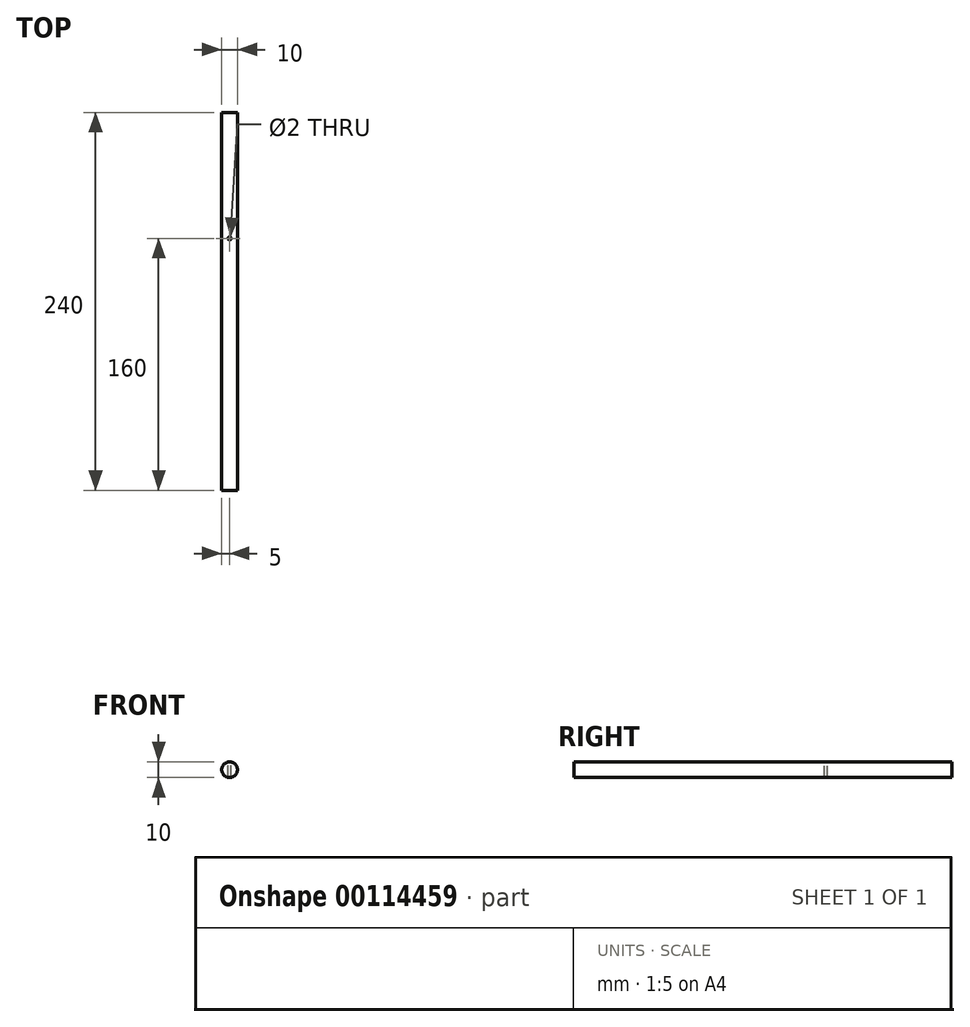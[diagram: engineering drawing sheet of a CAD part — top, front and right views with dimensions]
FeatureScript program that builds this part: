
annotation { "Feature Type Name" : "Feature", "Feature Type Description" : "" }
export const myFeature = defineFeature(function(context is Context, id is Id, definition is map)
    precondition{}
    {
        {
            var Q0;
            Q0=qCreatedBy(makeId("Front.planeOp"),FACE);
            var sketch = newSketch(context, id + "F0", { "sketchPlane" : qUnion([Q0])});
            skCircle(sketch, "E0", {"center": v(0, 0) * mm, "radius": 5 * mm});
            skSolve(sketch);
        }
        {
            var Q0;
            Q0 = qSketchRegion(id + "F0", true);
            extrude(context, id + "F1", {"entities" : qUnion([Q0]), "depth" : 240 * mm});
        }
        {
            var Q0;
            Q0=qCreatedBy(makeId("Top.planeOp"),FACE);
            cPlane(context, id + "F2", {"entities" : qUnion([Q0]), "cplaneType" : CPlaneType.OFFSET, "offset" : 5 * mm, "width" : 150 * mm, "height" : 150 * mm});
        }
        {
            var Q0;
            Q0=qCreatedBy(id+"F2.planeOp",FACE);
            var sketch = newSketch(context, id + "F3", { "sketchPlane" : qUnion([Q0])});
            skCircle(sketch, "E1", {"center": v(0, -80) * mm, "radius": 1 * mm});
            skSolve(sketch);
        }
        {
            var Q0;
            Q0 = qSketchRegion(id + "F3", true);
            extrude(context, id + "F4", {"entities" : qUnion([Q0]), "operationType" : NewBodyOperationType.REMOVE, "endBound" : BoundingType.THROUGH_ALL, "oppositeDirection" : true, "depth" : 25 * mm});
        }
    });
